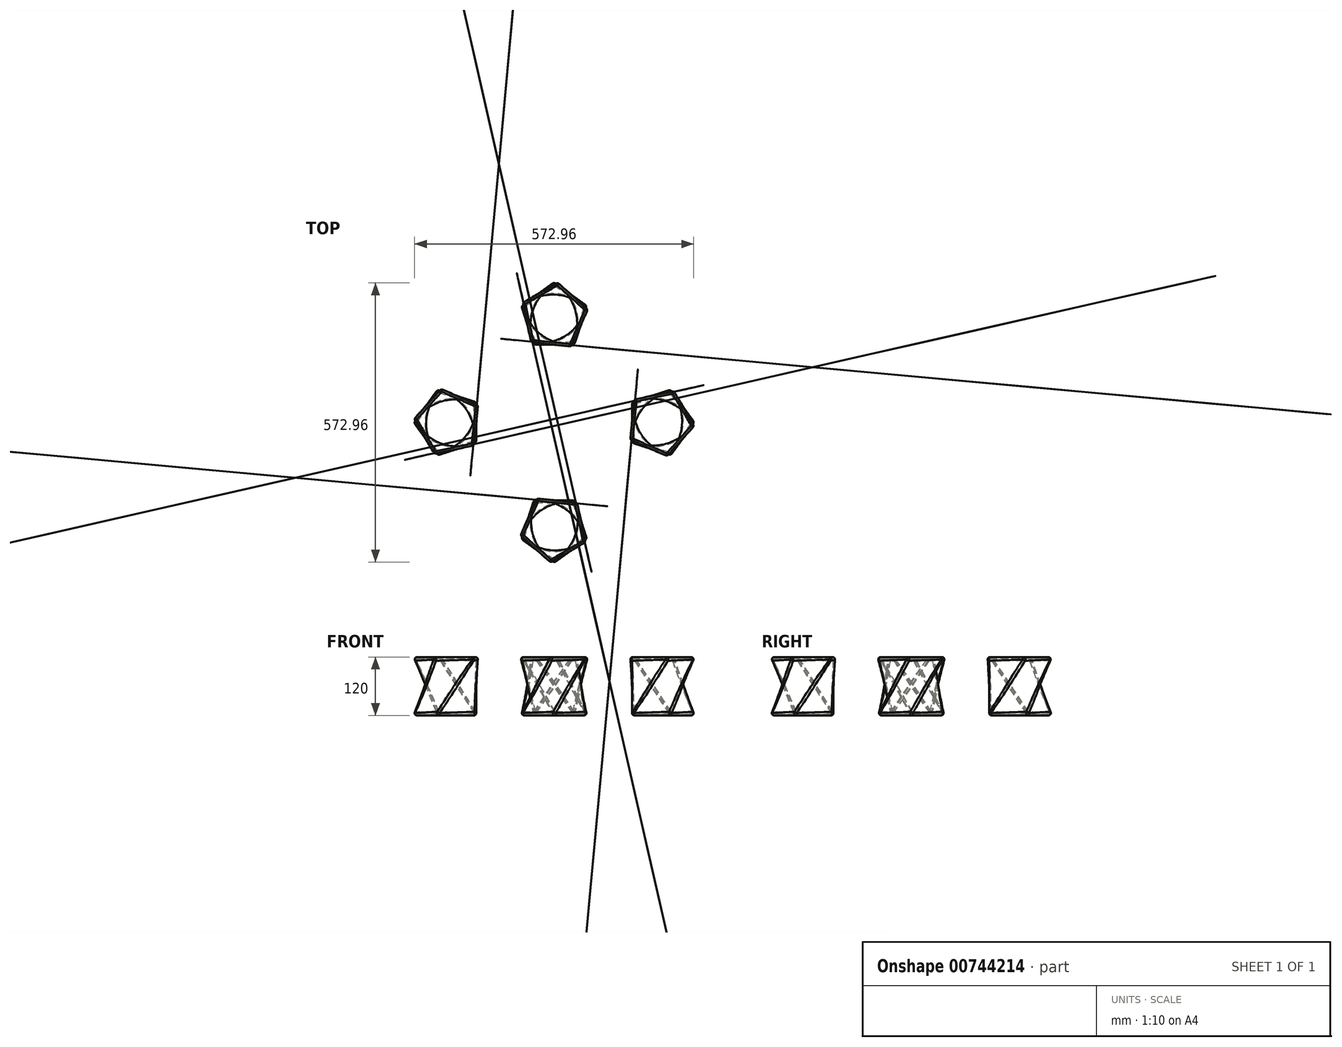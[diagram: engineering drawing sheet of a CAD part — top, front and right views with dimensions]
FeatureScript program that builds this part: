
annotation { "Feature Type Name" : "Feature", "Feature Type Description" : "" }
export const myFeature = defineFeature(function(context is Context, id is Id, definition is map)
    precondition{}
    {
        {
            var Q0;
            Q0=qCreatedBy(makeId("Top.planeOp"),FACE);
            cPlane(context, id + "F0", {"entities" : qUnion([Q0]), "cplaneType" : CPlaneType.OFFSET, "offset" : 120 * mm, "width" : 150 * mm, "height" : 150 * mm});
        }
        {
            var Q0;
            Q0=qCreatedBy(makeId("Top.planeOp"),FACE);
            var sketch = newSketch(context, id + "F1", { "sketchPlane" : qUnion([Q0])});
            skCircle(sketch, "E0.cCircle", {"center": v(0, 0) * mm, "radius": 59.2 * mm, "construction": true});
            skLineSegment(sketch, "E0.0", {"start": v(25.93, 68.43) * mm, "end": v(73.1, -3.51) * mm});
            skLineSegment(sketch, "E0.1", {"start": v(73.1, -3.51) * mm, "end": v(19.24, -70.6) * mm});
            skLineSegment(sketch, "E0.2", {"start": v(19.24, -70.6) * mm, "end": v(-61.2, -40.12) * mm});
            skLineSegment(sketch, "E0.3", {"start": v(-61.2, -40.12) * mm, "end": v(-57.07, 45.8) * mm});
            skLineSegment(sketch, "E0.4", {"start": v(-57.07, 45.8) * mm, "end": v(25.93, 68.43) * mm});
            skPoint(sketch, "E0.0.midPoint", {"position": v(49.51, 32.46) * mm});
            skSolve(sketch);
        }
        {
            var Q0;
            Q0=qCreatedBy(id+"F0.planeOp",FACE);
            var sketch = newSketch(context, id + "F2", { "sketchPlane" : qUnion([Q0])});
            skLineSegment(sketch, "E1.0.0", {"start": v(25.93, 68.43) * mm, "end": v(-57.07, 45.8) * mm});
            skLineSegment(sketch, "E1.0.1", {"start": v(-57.07, 45.8) * mm, "end": v(-61.2, -40.12) * mm});
            skLineSegment(sketch, "E1.0.2", {"start": v(-61.2, -40.12) * mm, "end": v(19.24, -70.6) * mm});
            skLineSegment(sketch, "E1.0.3", {"start": v(19.24, -70.6) * mm, "end": v(73.1, -3.51) * mm});
            skLineSegment(sketch, "E1.0.4", {"start": v(73.1, -3.51) * mm, "end": v(25.93, 68.43) * mm});
            skSolve(sketch);
        }
        {
            var Q0;
            Q0=makeQuery(id+"F1.imprint","IMPRINT",FACE,{"disambiguationData":[TD([[makeQuery(id+"F1.imprint","IMPRINT",EDGE,{"derivedFrom":sQuery(id+"F1.wireOp",EDGE,"E0.0")}),-1.0]])]});
            var Q1;
            Q1=makeQuery(id+"F2.imprint","IMPRINT",FACE,{"disambiguationData":[TD([[makeQuery(id+"F2.imprint","IMPRINT",EDGE,{"derivedFrom":sQuery(id+"F2.wireOp",EDGE,"E1.0.0")}),1.0]])]});
            var Q2;
            Q2=sQuery(id+"F1.wireOp",VERTEX,"E0.2.start");
            var Q3;
            Q3=sQuery(id+"F2.wireOp",VERTEX,"E1.0.3.end");
            loft(context, id + "F3", {"sheetProfilesArray" : [{ "sheetProfileEntities" : qUnion([Q0]) }, { "sheetProfileEntities" : qUnion([Q1]) }], "matchConnections" : true, "connections" : [{ "connectionEntities" : qUnion([Q2, Q3]), "connectionEdgeQueries" : qUnion([]), "connectionEdgeParameters" : [] }]});
        }
        {
            var Q0;
            Q0=makeQuery(id+"F3.opLoft","CAP_FACE",FACE,{"disambiguationData":[OSD([makeQuery(id+"F2.imprint","IMPRINT",FACE,{"disambiguationData":[TD([[makeQuery(id+"F2.imprint","IMPRINT",EDGE,{"derivedFrom":sQuery(id+"F2.wireOp",EDGE,"E1.0.0")}),1.0]])]})])],"isStart":true});
            var Q1;
            Q1=makeQuery(id+"F3.opLoft","CAP_FACE",FACE,{"disambiguationData":[OSD([makeQuery(id+"F1.imprint","IMPRINT",FACE,{"disambiguationData":[TD([[makeQuery(id+"F1.imprint","IMPRINT",EDGE,{"derivedFrom":sQuery(id+"F1.wireOp",EDGE,"E0.0")}),-1.0]])]})])],"isStart":true});
            var Q2;
            Q2=makeQuery(id+"F3.opLoft","SWEPT_EDGE",EDGE,{"disambiguationData":[OSD([sQuery(id+"F1.wireOp",EDGE,"E0.1"),sQuery(id+"F1.wireOp",EDGE,"E0.2"),sQuery(id+"F2.wireOp",EDGE,"E1.0.3"),sQuery(id+"F2.wireOp",EDGE,"E1.0.4")])]});
            var Q3;
            Q3=makeQuery(id+"F3.opLoft","SWEPT_EDGE",EDGE,{"disambiguationData":[OSD([sQuery(id+"F1.wireOp",EDGE,"E0.2"),sQuery(id+"F1.wireOp",EDGE,"E0.3"),sQuery(id+"F2.wireOp",EDGE,"E1.0.2"),sQuery(id+"F2.wireOp",EDGE,"E1.0.3")])]});
            var Q4;
            Q4=makeQuery(id+"F3.opLoft","SWEPT_EDGE",EDGE,{"disambiguationData":[OSD([sQuery(id+"F1.wireOp",EDGE,"E0.0"),sQuery(id+"F1.wireOp",EDGE,"E0.4"),sQuery(id+"F2.wireOp",EDGE,"E1.0.0"),sQuery(id+"F2.wireOp",EDGE,"E1.0.1")])]});
            var Q5;
            Q5=makeQuery(id+"F3.opLoft","SWEPT_EDGE",EDGE,{"disambiguationData":[OSD([sQuery(id+"F1.wireOp",EDGE,"E0.3"),sQuery(id+"F1.wireOp",EDGE,"E0.4"),sQuery(id+"F2.wireOp",EDGE,"E1.0.1"),sQuery(id+"F2.wireOp",EDGE,"E1.0.2")])]});
            var Q6;
            Q6=makeQuery(id+"F3.opLoft","SWEPT_EDGE",EDGE,{"disambiguationData":[OSD([sQuery(id+"F1.wireOp",EDGE,"E0.0"),sQuery(id+"F1.wireOp",EDGE,"E0.1"),sQuery(id+"F2.wireOp",EDGE,"E1.0.0"),sQuery(id+"F2.wireOp",EDGE,"E1.0.4")])]});
            fillet(context, id + "F4", {"entities" : qUnion([Q0, Q1, Q2, Q3, Q4, Q5, Q6]), "radius" : 5 * mm, "tangentPropagation" : true, "allowEdgeOverflow" : false});
        }
        {
            var Q0;
            Q0=makeQuery(id+"F3.opLoft","CAP_FACE",FACE,{"disambiguationData":[OSD([makeQuery(id+"F2.imprint","IMPRINT",FACE,{"disambiguationData":[TD([[makeQuery(id+"F2.imprint","IMPRINT",EDGE,{"derivedFrom":sQuery(id+"F2.wireOp",EDGE,"E1.0.0")}),1.0]])]})])],"isStart":true});
            shell(context, id + "F5", {"entities" : qUnion([Q0]), "thickness" : 2.5 * mm});
        }
        {
            var Q0;
            Q0=qCreatedBy(makeId("Front.planeOp"),FACE);
            var sketch = newSketch(context, id + "F6", { "sketchPlane" : qUnion([Q0])});
            skLineSegment(sketch, "E2", {"start": v(-217.1, 61.86) * mm, "end": v(-217.1, -10.8) * mm});
            skSolve(sketch);
        }
        {
            var Q0;
            Q0=makeQuery(id+"F3.opLoft","SWEPT_BODY",BODY,{"disambiguationData":[OSD([makeQuery(id+"F1.imprint","IMPRINT",FACE,{"disambiguationData":[TD([[makeQuery(id+"F1.imprint","IMPRINT",EDGE,{"derivedFrom":sQuery(id+"F1.wireOp",EDGE,"E0.0")}),-1.0]])]}),makeQuery(id+"F2.imprint","IMPRINT",FACE,{"disambiguationData":[TD([[makeQuery(id+"F2.imprint","IMPRINT",EDGE,{"derivedFrom":sQuery(id+"F2.wireOp",EDGE,"E1.0.0")}),1.0]])]})])]});
            var Q1;
            Q1=sQuery(id+"F6.wireOp",EDGE,"E2");
            circularPattern(context, id + "F7", {"entities" : qUnion([Q0]), "axis" : qUnion([Q1]), "angle" : 360 * degree, "instanceCount" : 4, "equalSpace" : true});
        }
    });
